# Revit family: M_Concrete-Rectangular-Column
name_source: partatom
category: Structural Columns
units: mm (PartAtom-declared; Revit-internal decimal feet)

## family parameters
Always export as geometry = No
Beam cutback in plan = From bounding box
Cut with Voids When Loaded = No
Display in Hidden Views = Edges Hidden by Other Members
Material for Model Behavior = Concrete
OmniClass Number = 23.25.30.11.14.11
OmniClass Title = Columns
Section Shape = Not Defined
Shared = No
Show family pre-cut in plan views = Yes

## types (7) — shared parameters

## per-type parameters (varying)
| type | b | h |
| 300 x 450mm | 300 mm | 450 mm  [stored 1.47638 ft] |
| 450 x 600mm | 450 mm  [stored 1.47638 ft] | 600 mm |
| 600 x 750mm | 600 mm | 750 mm |
| C2 | 1600 mm | 1600 mm |
| C4 | 1500 mm | 2200 mm |
| C3 | 1200 mm | 2100 mm |
| C1 | 1300 mm | 2000 mm |

note: [stored X ft] marks values corroborated as IEEE doubles in the binary element streams (Revit-internal decimal feet)

## geometry (parser evidence)
native form markers: Sweep x1
no freeform markers — native parametric forms only
